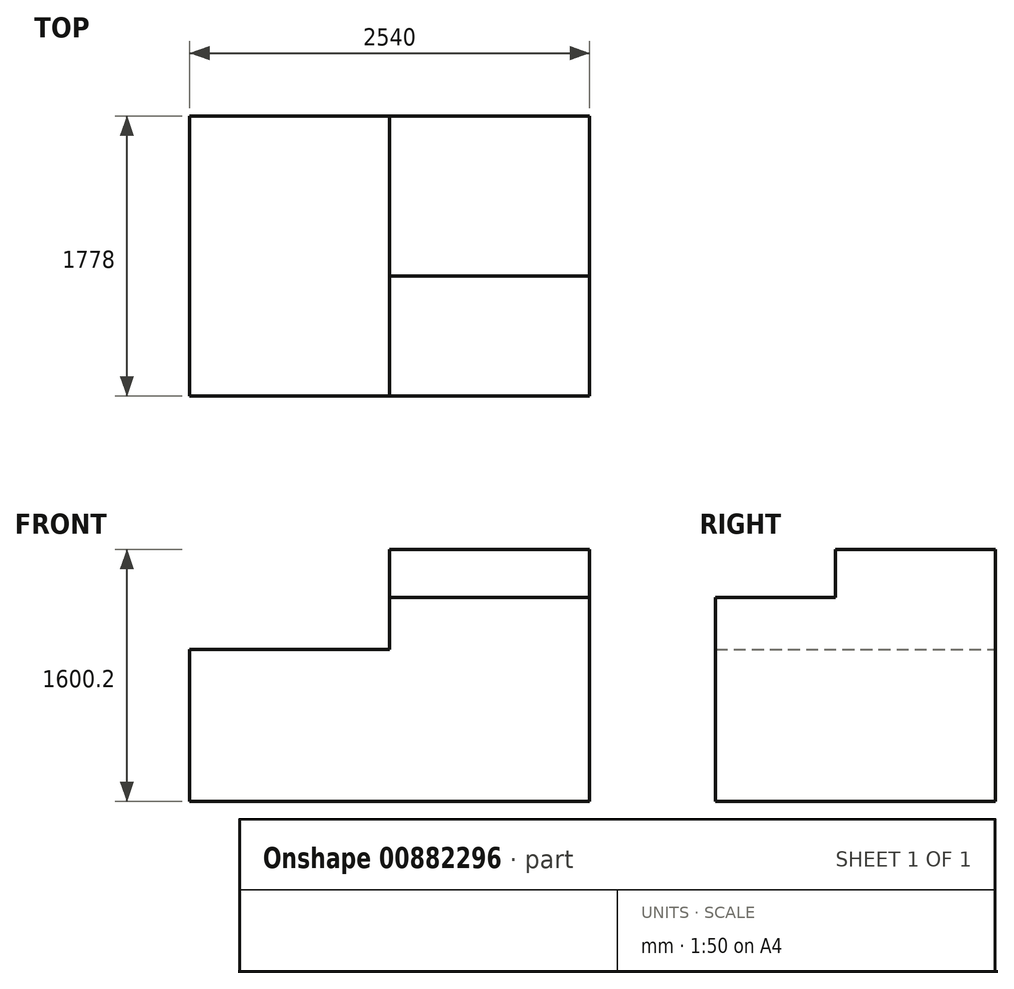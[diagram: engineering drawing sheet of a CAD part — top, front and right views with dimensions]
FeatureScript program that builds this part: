
annotation { "Feature Type Name" : "Feature", "Feature Type Description" : "" }
export const myFeature = defineFeature(function(context is Context, id is Id, definition is map)
    precondition{}
    {
        {
            var Q0;
            Q0=qCreatedBy(makeId("Top.planeOp"),FACE);
            var sketch = newSketch(context, id + "F0", { "sketchPlane" : qUnion([Q0])});
            skLineSegment(sketch, "E0", {"start": v(0, -889) * mm, "end": v(-1270, -889) * mm});
            skLineSegment(sketch, "E1", {"start": v(-1270, -889) * mm, "end": v(-1270, 889) * mm});
            skLineSegment(sketch, "E2", {"start": v(-1270, 889) * mm, "end": v(-1016, 889) * mm});
            skLineSegment(sketch, "E3", {"start": v(-1016, 889) * mm, "end": v(1270, 889) * mm});
            skLineSegment(sketch, "E4", {"start": v(1270, 889) * mm, "end": v(1270, -889) * mm});
            skLineSegment(sketch, "E5", {"start": v(1270, -889) * mm, "end": v(0, -889) * mm});
            skSolve(sketch);
        }
        {
            var Q0;
            Q0=makeQuery(id+"F0.imprint","IMPRINT",FACE,{"disambiguationData":[TD([[makeQuery(id+"F0.imprint","IMPRINT",EDGE,{"derivedFrom":sQuery(id+"F0.wireOp",EDGE,"E0")}),-1.0]])]});
            extrude(context, id + "F1", {"entities" : qUnion([Q0]), "depth" : 965.2 * mm, "offsetDistance" : 25.4 * mm});
        }
        {
            var Q0;
            Q0=makeQuery(id+"F1.opExtrude","CAP_FACE",FACE,{"disambiguationData":[OSD([sQuery(id+"F0.wireOp",EDGE,"E0"),sQuery(id+"F0.wireOp",EDGE,"E1"),sQuery(id+"F0.wireOp",EDGE,"E2"),sQuery(id+"F0.wireOp",EDGE,"E3"),sQuery(id+"F0.wireOp",EDGE,"E4"),sQuery(id+"F0.wireOp",EDGE,"E5")])],"isStart":false});
            var sketch = newSketch(context, id + "F2", { "sketchPlane" : qUnion([Q0])});
            skLineSegment(sketch, "E6", {"start": v(-1270, 889) * mm, "end": v(-1270, -889) * mm});
            skLineSegment(sketch, "E7", {"start": v(1270, 889) * mm, "end": v(1270, -889) * mm});
            skLineSegment(sketch, "E8", {"start": v(1270, -889) * mm, "end": v(0, -889) * mm});
            skLineSegment(sketch, "E9", {"start": v(0, -889) * mm, "end": v(0, 889) * mm});
            skLineSegment(sketch, "E10", {"start": v(0, 889) * mm, "end": v(1270, 889) * mm});
            skSolve(sketch);
        }
        {
            var Q0;
            Q0=makeQuery(id+"F2.imprint","IMPRINT",FACE,{"disambiguationData":[TD([[makeQuery(id+"F2.imprint","IMPRINT",EDGE,{"derivedFrom":sQuery(id+"F2.wireOp",EDGE,"E7")}),-1.0]])]});
            extrude(context, id + "F3", {"entities" : qUnion([Q0]), "operationType" : NewBodyOperationType.ADD, "depth" : 330.2 * mm, "offsetDistance" : 25.4 * mm});
        }
        {
            var Q0;
            Q0=makeQuery(id+"F3.opExtrude","CAP_FACE",FACE,{"disambiguationData":[OSD([sQuery(id+"F2.wireOp",EDGE,"E7"),sQuery(id+"F2.wireOp",EDGE,"E8"),sQuery(id+"F2.wireOp",EDGE,"E9"),sQuery(id+"F2.wireOp",EDGE,"E10")])],"isStart":false});
            var sketch = newSketch(context, id + "F4", { "sketchPlane" : qUnion([Q0])});
            skLineSegment(sketch, "E11", {"start": v(0, 889) * mm, "end": v(0, -127) * mm});
            skLineSegment(sketch, "E12", {"start": v(0, -127) * mm, "end": v(1270, -127) * mm});
            skLineSegment(sketch, "E13", {"start": v(1270, -127) * mm, "end": v(1270, 889) * mm});
            skLineSegment(sketch, "E14", {"start": v(1270, 889) * mm, "end": v(0, 889) * mm});
            skSolve(sketch);
        }
        {
            var Q0;
            Q0=makeQuery(id+"F4.imprint","IMPRINT",FACE,{"disambiguationData":[TD([[makeQuery(id+"F4.imprint","IMPRINT",EDGE,{"derivedFrom":sQuery(id+"F4.wireOp",EDGE,"E11")}),-1.0]])]});
            extrude(context, id + "F5", {"entities" : qUnion([Q0]), "operationType" : NewBodyOperationType.ADD, "depth" : 304.8 * mm, "offsetDistance" : 25.4 * mm});
        }
    });
